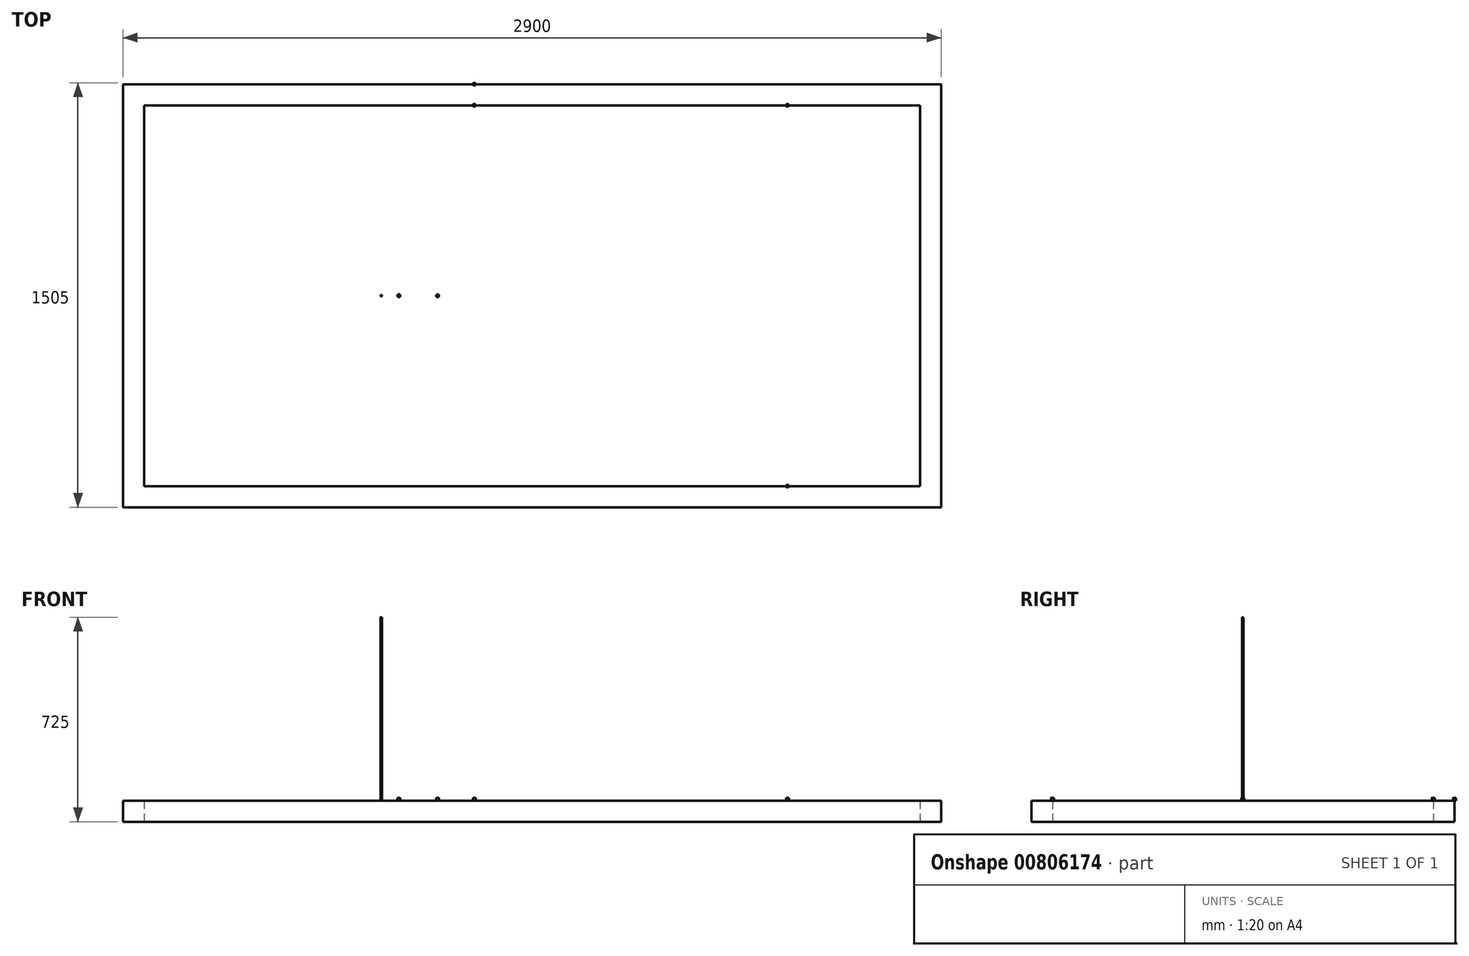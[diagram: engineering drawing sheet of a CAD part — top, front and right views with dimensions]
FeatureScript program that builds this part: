
annotation { "Feature Type Name" : "Feature", "Feature Type Description" : "" }
export const myFeature = defineFeature(function(context is Context, id is Id, definition is map)
    precondition{}
    {
        {
            var Q0;
            Q0=qCreatedBy(makeId("Top.planeOp"),FACE);
            var sketch = newSketch(context, id + "F0", { "sketchPlane" : qUnion([Q0])});
            skPoint(sketch, "E0.middle", {"position": v(0, 0) * mm});
            skLineSegment(sketch, "E1.bottom", {"start": v(-1450, -750) * mm, "end": v(1450, -750) * mm});
            skLineSegment(sketch, "E1.top", {"start": v(-1450, 750) * mm, "end": v(1450, 750) * mm});
            skLineSegment(sketch, "E1.left", {"start": v(-1450, -750) * mm, "end": v(-1450, 750) * mm});
            skLineSegment(sketch, "E1.right", {"start": v(1450, -750) * mm, "end": v(1450, 750) * mm});
            skPoint(sketch, "E2.endSnap0", {"position": v(-1450, 0) * mm});
            skLineSegment(sketch, "E3.0", {"start": v(-1375, -675) * mm, "end": v(-1375, 675) * mm});
            skLineSegment(sketch, "E3.1", {"start": v(-1375, -675) * mm, "end": v(1375, -675) * mm});
            skLineSegment(sketch, "E3.2", {"start": v(1375, -675) * mm, "end": v(1375, 675) * mm});
            skLineSegment(sketch, "E3.3", {"start": v(-1375, 675) * mm, "end": v(1375, 675) * mm});
            skLineSegment(sketch, "E4", {"start": v(-1375, -675) * mm, "end": v(-435, -675) * mm});
            skLineSegment(sketch, "E5.bottom", {"start": v(-435, -675) * mm, "end": v(-510, -675) * mm});
            skLineSegment(sketch, "E5.top", {"start": v(-435, 675) * mm, "end": v(-510, 675) * mm});
            skLineSegment(sketch, "E5.left", {"start": v(-435, -675) * mm, "end": v(-435, 675) * mm});
            skLineSegment(sketch, "E5.right", {"start": v(-510, -675) * mm, "end": v(-510, 675) * mm});
            skLineSegment(sketch, "E6", {"start": v(1375, -675) * mm, "end": v(435, -675) * mm});
            skLineSegment(sketch, "E7.bottom", {"start": v(435, -675) * mm, "end": v(510, -675) * mm});
            skLineSegment(sketch, "E7.top", {"start": v(435, 675) * mm, "end": v(510, 675) * mm});
            skLineSegment(sketch, "E7.left", {"start": v(435, -675) * mm, "end": v(435, 675) * mm});
            skLineSegment(sketch, "E7.right", {"start": v(510, -675) * mm, "end": v(510, 675) * mm});
            skSolve(sketch);
        }
        {
            var Q0;
            Q0=qSketchRegion(id+"F0",true);
            var Q1;
            Q1=makeQuery(id+"F0.imprint","IMPRINT",FACE,{"disambiguationData":[TD([[makeQuery(id+"F0.imprint","IMPRINT",EDGE,{"derivedFrom":sQuery(id+"F0.wireOp",EDGE,"E5.bottom")}),-1.0]])]});
            var Q2;
            Q2=makeQuery(id+"F0.imprint","IMPRINT",FACE,{"disambiguationData":[TD([[makeQuery(id+"F0.imprint","IMPRINT",EDGE,{"derivedFrom":sQuery(id+"F0.wireOp",EDGE,"E7.bottom")}),1.0]])]});
            extrude(context, id + "F1", {"entities" : qUnion([Q0, Q1, Q2]), "depth" : 75 * mm, "offsetDistance" : 25 * mm});
        }
        {
            var Q0;
            Q0=makeQuery(id+"F1.opExtrude","CAP_FACE",FACE,{"disambiguationData":[OSD([sQuery(id+"F0.wireOp",EDGE,"E1.bottom"),sQuery(id+"F0.wireOp",EDGE,"E1.top"),sQuery(id+"F0.wireOp",EDGE,"E1.left"),sQuery(id+"F0.wireOp",EDGE,"E1.right"),sQuery(id+"F0.wireOp",EDGE,"E3.0"),sQuery(id+"F0.wireOp",EDGE,"E3.1"),sQuery(id+"F0.wireOp",EDGE,"E3.2"),sQuery(id+"F0.wireOp",EDGE,"E3.3"),sQuery(id+"F0.wireOp",EDGE,"E4"),sQuery(id+"F0.wireOp",EDGE,"E5.left"),sQuery(id+"F0.wireOp",EDGE,"E5.right"),sQuery(id+"F0.wireOp",EDGE,"E6"),sQuery(id+"F0.wireOp",EDGE,"E7.left"),sQuery(id+"F0.wireOp",EDGE,"E7.right")])],"isStart":false});
            var sketch = newSketch(context, id + "F2", { "sketchPlane" : qUnion([Q0])});
            skLineSegment(sketch, "E8", {"start": v(-435, 0) * mm, "end": v(-472.5, 0) * mm});
            skCircle(sketch, "E9", {"center": v(-472.5, 0) * mm, "radius": 5 * mm});
            skLineSegment(sketch, "E10", {"start": v(-435, 0) * mm, "end": v(-335, 0) * mm});
            skCircle(sketch, "E11", {"center": v(-335, 0) * mm, "radius": 5 * mm});
            skLineSegment(sketch, "E12", {"start": v(-1375, 675) * mm, "end": v(905, 675) * mm});
            skCircle(sketch, "E13", {"center": v(905, 675) * mm, "radius": 5 * mm});
            skLineSegment(sketch, "E14", {"start": v(-1375, -675) * mm, "end": v(905, -675) * mm});
            skCircle(sketch, "E15", {"center": v(905, -675) * mm, "radius": 5 * mm});
            skLineSegment(sketch, "E16", {"start": v(905, 675) * mm, "end": v(-205, 675) * mm});
            skCircle(sketch, "E17", {"center": v(-205, 675) * mm, "radius": 5 * mm});
            skLineSegment(sketch, "E18", {"start": v(-205, 675) * mm, "end": v(-205, 750) * mm});
            skCircle(sketch, "E19", {"center": v(-205, 750) * mm, "radius": 5 * mm});
            skSolve(sketch);
        }
        {
            var Q0;
            Q0=qSketchRegion(id+"F2",true);
            extrude(context, id + "F3", {"entities" : qUnion([Q0]), "operationType" : NewBodyOperationType.ADD, "depth" : 10 * mm, "offsetDistance" : 25 * mm});
        }
        {
            var Q0;
            Q0=qSketchRegion(id+"F2",true);
            extrude(context, id + "F4", {"entities" : qUnion([Q0]), "depth" : 10 * mm, "offsetDistance" : 25 * mm});
        }
        {
            var Q0;
            Q0=makeQuery(id+"F1.opExtrude","CAP_FACE",FACE,{"disambiguationData":[OSD([sQuery(id+"F0.wireOp",EDGE,"E1.bottom"),sQuery(id+"F0.wireOp",EDGE,"E1.top"),sQuery(id+"F0.wireOp",EDGE,"E1.left"),sQuery(id+"F0.wireOp",EDGE,"E1.right"),sQuery(id+"F0.wireOp",EDGE,"E3.0"),sQuery(id+"F0.wireOp",EDGE,"E3.1"),sQuery(id+"F0.wireOp",EDGE,"E3.2"),sQuery(id+"F0.wireOp",EDGE,"E3.3"),sQuery(id+"F0.wireOp",EDGE,"E4"),sQuery(id+"F0.wireOp",EDGE,"E5.left"),sQuery(id+"F0.wireOp",EDGE,"E5.right"),sQuery(id+"F0.wireOp",EDGE,"E6"),sQuery(id+"F0.wireOp",EDGE,"E7.left"),sQuery(id+"F0.wireOp",EDGE,"E7.right")])],"isStart":false});
            var sketch = newSketch(context, id + "F5", { "sketchPlane" : qUnion([Q0])});
            skLineSegment(sketch, "E20", {"start": v(-535, 0) * mm, "end": v(-435, 0) * mm});
            skCircle(sketch, "E21", {"center": v(-535, 0) * mm, "radius": 2.5 * mm});
            skSolve(sketch);
        }
        {
            var Q0;
            Q0=qSketchRegion(id+"F5",true);
            extrude(context, id + "F6", {"entities" : qUnion([Q0]), "operationType" : NewBodyOperationType.ADD, "depth" : 650 * mm, "offsetDistance" : 25 * mm});
        }
    });
